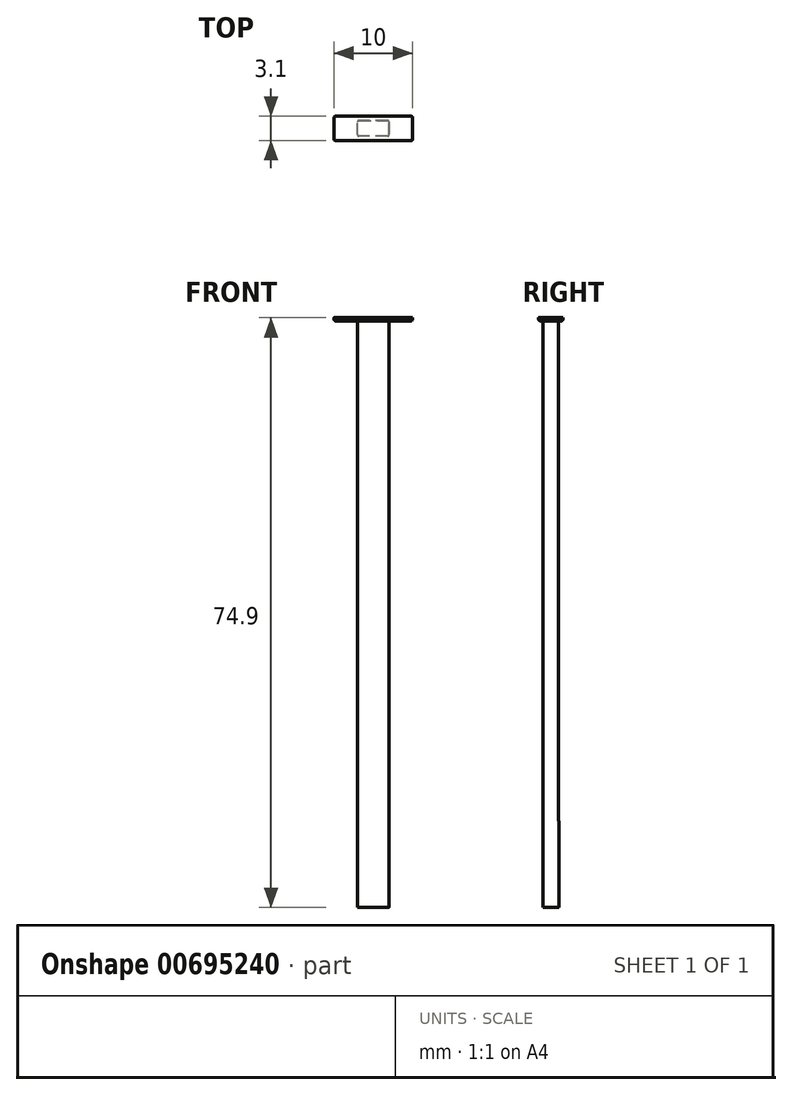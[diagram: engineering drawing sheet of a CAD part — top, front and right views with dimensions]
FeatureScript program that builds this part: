
annotation { "Feature Type Name" : "Feature", "Feature Type Description" : "" }
export const myFeature = defineFeature(function(context is Context, id is Id, definition is map)
    precondition{}
    {
        {
            var Q0;
            Q0=qCreatedBy(makeId("Top.planeOp"),FACE);
            var sketch = newSketch(context, id + "F0", { "sketchPlane" : qUnion([Q0])});
            skLineSegment(sketch, "E0.bottom", {"start": v(2, -1) * mm, "end": v(-2, -1) * mm});
            skLineSegment(sketch, "E0.top", {"start": v(2, 1) * mm, "end": v(-2, 1) * mm});
            skLineSegment(sketch, "E0.left", {"start": v(2, -1) * mm, "end": v(2, 1) * mm});
            skLineSegment(sketch, "E0.right", {"start": v(-2, -1) * mm, "end": v(-2, 1) * mm});
            skPoint(sketch, "E0.middle", {"position": v(0, 0) * mm});
            skSolve(sketch);
        }
        {
            var Q0;
            Q0 = qSketchRegion(id + "F0", true);
            extrude(context, id + "F1", {"entities" : qUnion([Q0]), "depth" : 11 * mm, "offsetDistance" : 25 * mm});
        }
        {
            var Q0;
            Q0=makeQuery(id+"F1.opExtrude","SWEPT_EDGE",EDGE,{"disambiguationData":[OSD([sQuery(id+"F0.wireOp",EDGE,"E0.top"),sQuery(id+"F0.wireOp",EDGE,"E0.right")])]});
            var Q1;
            Q1=makeQuery(id+"F1.opExtrude","SWEPT_EDGE",EDGE,{"disambiguationData":[OSD([sQuery(id+"F0.wireOp",EDGE,"E0.top"),sQuery(id+"F0.wireOp",EDGE,"E0.left")])]});
            var Q2;
            Q2=makeQuery(id+"F1.opExtrude","SWEPT_EDGE",EDGE,{"disambiguationData":[OSD([sQuery(id+"F0.wireOp",EDGE,"E0.bottom"),sQuery(id+"F0.wireOp",EDGE,"E0.right")])]});
            var Q3;
            Q3=makeQuery(id+"F1.opExtrude","SWEPT_EDGE",EDGE,{"disambiguationData":[OSD([sQuery(id+"F0.wireOp",EDGE,"E0.bottom"),sQuery(id+"F0.wireOp",EDGE,"E0.left")])]});
            fillet(context, id + "F2", {"entities" : qUnion([Q0, Q1, Q2, Q3]), "radius" : 0.2 * mm, "tangentPropagation" : true, "allowEdgeOverflow" : false});
        }
        {
            var Q0;
            Q0=makeQuery(id+"F1.opExtrude","CAP_FACE",FACE,{"disambiguationData":[OSD([sQuery(id+"F0.wireOp",EDGE,"E0.bottom"),sQuery(id+"F0.wireOp",EDGE,"E0.top"),sQuery(id+"F0.wireOp",EDGE,"E0.left"),sQuery(id+"F0.wireOp",EDGE,"E0.right")])],"isStart":false});
            var sketch = newSketch(context, id + "F3", { "sketchPlane" : qUnion([Q0])});
            skLineSegment(sketch, "E1.bottom", {"start": v(2, -1) * mm, "end": v(-2, -1) * mm});
            skLineSegment(sketch, "E1.top", {"start": v(2, 1) * mm, "end": v(-2, 1) * mm});
            skLineSegment(sketch, "E1.left", {"start": v(2, -1) * mm, "end": v(2, 1) * mm});
            skLineSegment(sketch, "E1.right", {"start": v(-2, -1) * mm, "end": v(-2, 1) * mm});
            skPoint(sketch, "E1.middle", {"position": v(0, 0) * mm});
            skSolve(sketch);
        }
        {
            var Q0;
            Q0 = qSketchRegion(id + "F3", true);
            extrude(context, id + "F4", {"entities" : qUnion([Q0]), "operationType" : NewBodyOperationType.ADD, "depth" : 63.5 * mm, "offsetDistance" : 25 * mm});
        }
        {
            var Q0;
            Q0=makeQuery(id+"F4.opExtrude","SWEPT_EDGE",EDGE,{"disambiguationData":[OSD([sQuery(id+"F3.wireOp",EDGE,"E1.top"),sQuery(id+"F3.wireOp",EDGE,"E1.right")])]});
            var Q1;
            Q1=makeQuery(id+"F4.opExtrude","SWEPT_EDGE",EDGE,{"disambiguationData":[OSD([sQuery(id+"F3.wireOp",EDGE,"E1.bottom"),sQuery(id+"F3.wireOp",EDGE,"E1.right")])]});
            var Q2;
            Q2=makeQuery(id+"F4.opExtrude","SWEPT_EDGE",EDGE,{"disambiguationData":[OSD([sQuery(id+"F3.wireOp",EDGE,"E1.top"),sQuery(id+"F3.wireOp",EDGE,"E1.left")])]});
            var Q3;
            Q3=makeQuery(id+"F4.opExtrude","SWEPT_EDGE",EDGE,{"disambiguationData":[OSD([sQuery(id+"F3.wireOp",EDGE,"E1.bottom"),sQuery(id+"F3.wireOp",EDGE,"E1.left")])]});
            fillet(context, id + "F5", {"entities" : qUnion([Q0, Q1, Q2, Q3]), "radius" : 0.2 * mm, "tangentPropagation" : true, "allowEdgeOverflow" : false});
        }
        {
            var Q0;
            Q0=makeQuery(id+"F4.opExtrude","CAP_FACE",FACE,{"disambiguationData":[OSD([sQuery(id+"F3.wireOp",EDGE,"E1.bottom"),sQuery(id+"F3.wireOp",EDGE,"E1.top"),sQuery(id+"F3.wireOp",EDGE,"E1.left"),sQuery(id+"F3.wireOp",EDGE,"E1.right")])],"isStart":false});
            var sketch = newSketch(context, id + "F6", { "sketchPlane" : qUnion([Q0])});
            skLineSegment(sketch, "E2.bottom", {"start": v(5, -1.55) * mm, "end": v(-5, -1.55) * mm});
            skLineSegment(sketch, "E2.top", {"start": v(5, 1.55) * mm, "end": v(-5, 1.55) * mm});
            skLineSegment(sketch, "E2.left", {"start": v(5, -1.55) * mm, "end": v(5, 1.55) * mm});
            skLineSegment(sketch, "E2.right", {"start": v(-5, -1.55) * mm, "end": v(-5, 1.55) * mm});
            skPoint(sketch, "E2.middle", {"position": v(0, 0) * mm});
            skSolve(sketch);
        }
        {
            var Q0;
            Q0 = qSketchRegion(id + "F6", true);
            extrude(context, id + "F7", {"entities" : qUnion([Q0]), "operationType" : NewBodyOperationType.ADD, "depth" : 0.4 * mm, "offsetDistance" : 25 * mm});
        }
        {
            var Q0;
            Q0=makeQuery(id+"F7.opExtrude","SWEPT_EDGE",EDGE,{"disambiguationData":[OSD([sQuery(id+"F6.wireOp",EDGE,"E2.bottom"),sQuery(id+"F6.wireOp",EDGE,"E2.right")])]});
            var Q1;
            Q1=makeQuery(id+"F7.opExtrude","SWEPT_EDGE",EDGE,{"disambiguationData":[OSD([sQuery(id+"F6.wireOp",EDGE,"E2.bottom"),sQuery(id+"F6.wireOp",EDGE,"E2.left")])]});
            var Q2;
            Q2=makeQuery(id+"F7.opExtrude","CAP_EDGE",EDGE,{"disambiguationData":[OSD([sQuery(id+"F6.wireOp",EDGE,"E2.bottom")])],"isStart":true});
            var Q3;
            Q3=makeQuery(id+"F7.opExtrude","CAP_EDGE",EDGE,{"disambiguationData":[OSD([sQuery(id+"F6.wireOp",EDGE,"E2.right")])],"isStart":true});
            var Q4;
            Q4=makeQuery(id+"F7.opExtrude","CAP_EDGE",EDGE,{"disambiguationData":[OSD([sQuery(id+"F6.wireOp",EDGE,"E2.top")])],"isStart":true});
            var Q5;
            Q5=makeQuery(id+"F7.opExtrude","SWEPT_EDGE",EDGE,{"disambiguationData":[OSD([sQuery(id+"F6.wireOp",EDGE,"E2.top"),sQuery(id+"F6.wireOp",EDGE,"E2.right")])]});
            var Q6;
            Q6=makeQuery(id+"F7.opExtrude","SWEPT_EDGE",EDGE,{"disambiguationData":[OSD([sQuery(id+"F6.wireOp",EDGE,"E2.top"),sQuery(id+"F6.wireOp",EDGE,"E2.left")])]});
            var Q7;
            Q7=makeQuery(id+"F7.opExtrude","CAP_EDGE",EDGE,{"disambiguationData":[OSD([sQuery(id+"F6.wireOp",EDGE,"E2.left")])],"isStart":true});
            fillet(context, id + "F8", {"entities" : qUnion([Q0, Q1, Q2, Q3, Q4, Q5, Q6, Q7]), "radius" : 0.2 * mm, "tangentPropagation" : true, "allowEdgeOverflow" : false});
        }
    });
